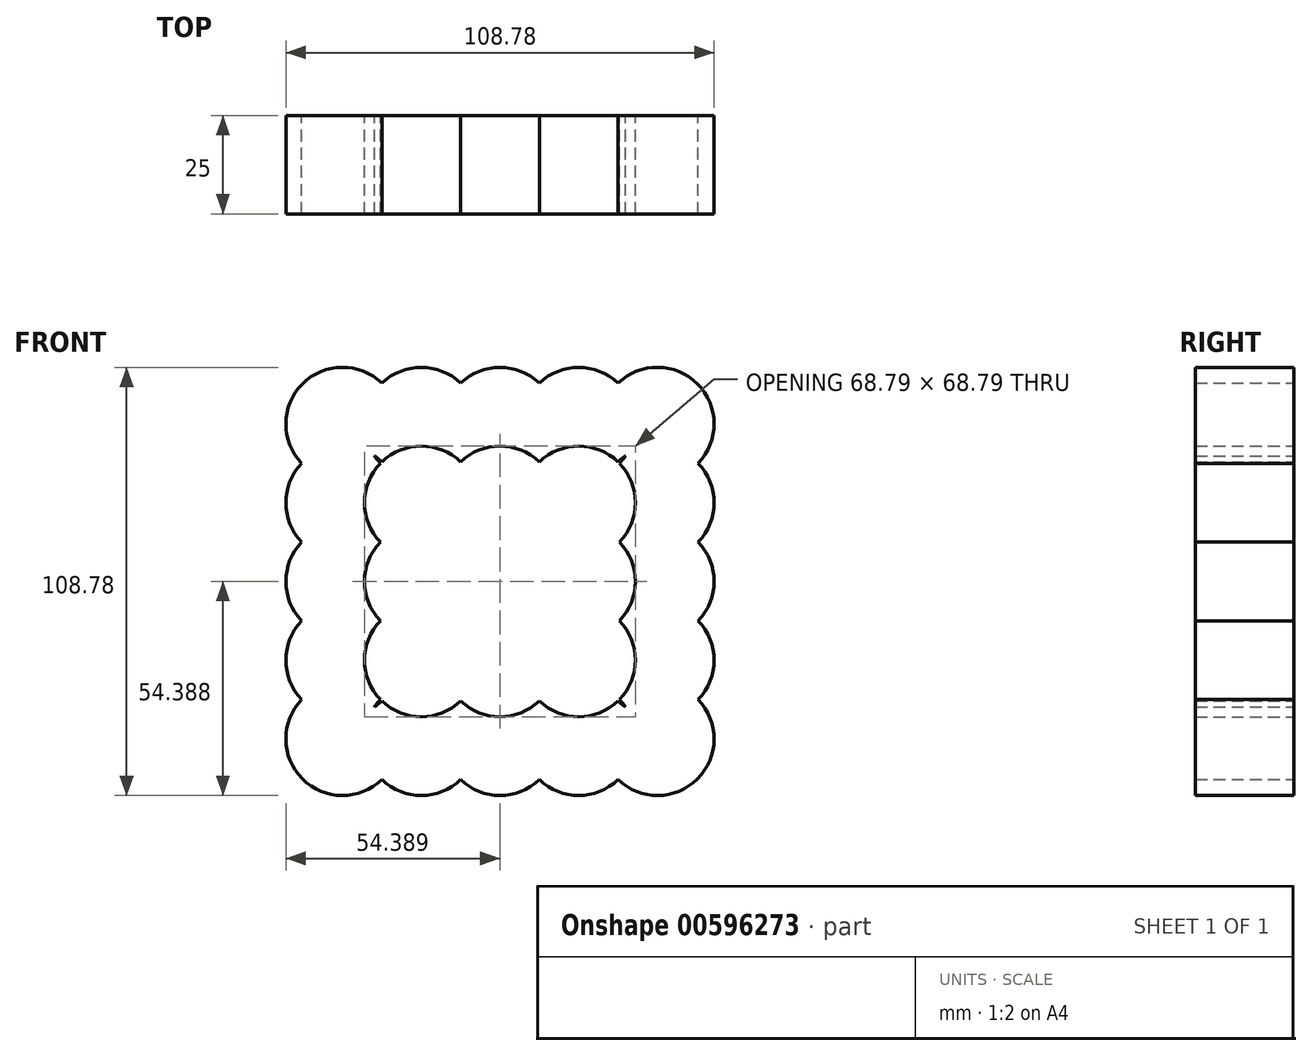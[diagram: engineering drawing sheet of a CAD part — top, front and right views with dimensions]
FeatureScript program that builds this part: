
annotation { "Feature Type Name" : "Feature", "Feature Type Description" : "" }
export const myFeature = defineFeature(function(context is Context, id is Id, definition is map)
    precondition{}
    {
        {
            var Q0;
            Q0=qCreatedBy(makeId("Front.planeOp"),FACE);
            var sketch = newSketch(context, id + "F0", { "sketchPlane" : qUnion([Q0])});
            skCircle(sketch, "E0", {"center": v(-95.76, -32.97) * mm, "radius": 14.4 * mm});
            skCircle(sketch, "E1.0.1.0", {"center": v(-95.76, -12.97) * mm, "radius": 14.4 * mm});
            skCircle(sketch, "E1.1.0.0", {"center": v(-75.76, -32.97) * mm, "radius": 14.4 * mm});
            skCircle(sketch, "E1.1.1.0", {"center": v(-75.76, -12.97) * mm, "radius": 14.4 * mm});
            skCircle(sketch, "E1.2.0.0", {"center": v(-55.76, -32.97) * mm, "radius": 14.4 * mm});
            skCircle(sketch, "E1.2.1.0", {"center": v(-55.76, -12.97) * mm, "radius": 14.4 * mm});
            skLineSegment(sketch, "E1.direction1", {"start": v(-95.76, -32.97) * mm, "end": v(-75.76, -32.97) * mm, "construction": true});
            skLineSegment(sketch, "E1.direction2", {"start": v(-95.76, -32.97) * mm, "end": v(-95.76, -12.97) * mm, "construction": true});
            skCircle(sketch, "E2.0.3.0", {"center": v(-35.76, -32.97) * mm, "radius": 14.4 * mm});
            skCircle(sketch, "E2.0.3.1", {"center": v(-35.76, -12.97) * mm, "radius": 14.4 * mm});
            skCircle(sketch, "E2.0.4.0", {"center": v(-15.76, -32.97) * mm, "radius": 14.4 * mm});
            skCircle(sketch, "E2.0.4.1", {"center": v(-15.76, -12.97) * mm, "radius": 14.4 * mm});
            skCircle(sketch, "E3.0.0.2", {"center": v(-95.76, 7.03) * mm, "radius": 14.4 * mm});
            skCircle(sketch, "E3.0.0.3", {"center": v(-95.76, 27.03) * mm, "radius": 14.4 * mm});
            skCircle(sketch, "E3.0.0.4", {"center": v(-95.76, 47.03) * mm, "radius": 14.4 * mm});
            skCircle(sketch, "E3.0.1.2", {"center": v(-75.76, 7.03) * mm, "radius": 14.4 * mm});
            skCircle(sketch, "E3.0.1.3", {"center": v(-75.76, 27.03) * mm, "radius": 14.4 * mm});
            skCircle(sketch, "E3.0.1.4", {"center": v(-75.76, 47.03) * mm, "radius": 14.4 * mm});
            skCircle(sketch, "E3.0.2.2", {"center": v(-55.76, 7.03) * mm, "radius": 14.4 * mm});
            skCircle(sketch, "E3.0.2.3", {"center": v(-55.76, 27.03) * mm, "radius": 14.4 * mm});
            skCircle(sketch, "E3.0.2.4", {"center": v(-55.76, 47.03) * mm, "radius": 14.4 * mm});
            skCircle(sketch, "E3.0.3.2", {"center": v(-35.76, 7.03) * mm, "radius": 14.4 * mm});
            skCircle(sketch, "E3.0.3.3", {"center": v(-35.76, 27.03) * mm, "radius": 14.4 * mm});
            skCircle(sketch, "E3.0.3.4", {"center": v(-35.76, 47.03) * mm, "radius": 14.4 * mm});
            skCircle(sketch, "E3.0.4.2", {"center": v(-15.76, 7.03) * mm, "radius": 14.4 * mm});
            skCircle(sketch, "E3.0.4.3", {"center": v(-15.76, 27.03) * mm, "radius": 14.4 * mm});
            skCircle(sketch, "E3.0.4.4", {"center": v(-15.76, 47.03) * mm, "radius": 14.4 * mm});
            skSolve(sketch);
        }
        {
            var Q0;
            Q0 = qSketchRegion(id + "F0", true);
            extrude(context, id + "F1", {"entities" : qUnion([Q0]), "depth" : 25 * mm, "offsetDistance" : 25 * mm});
        }
    });
